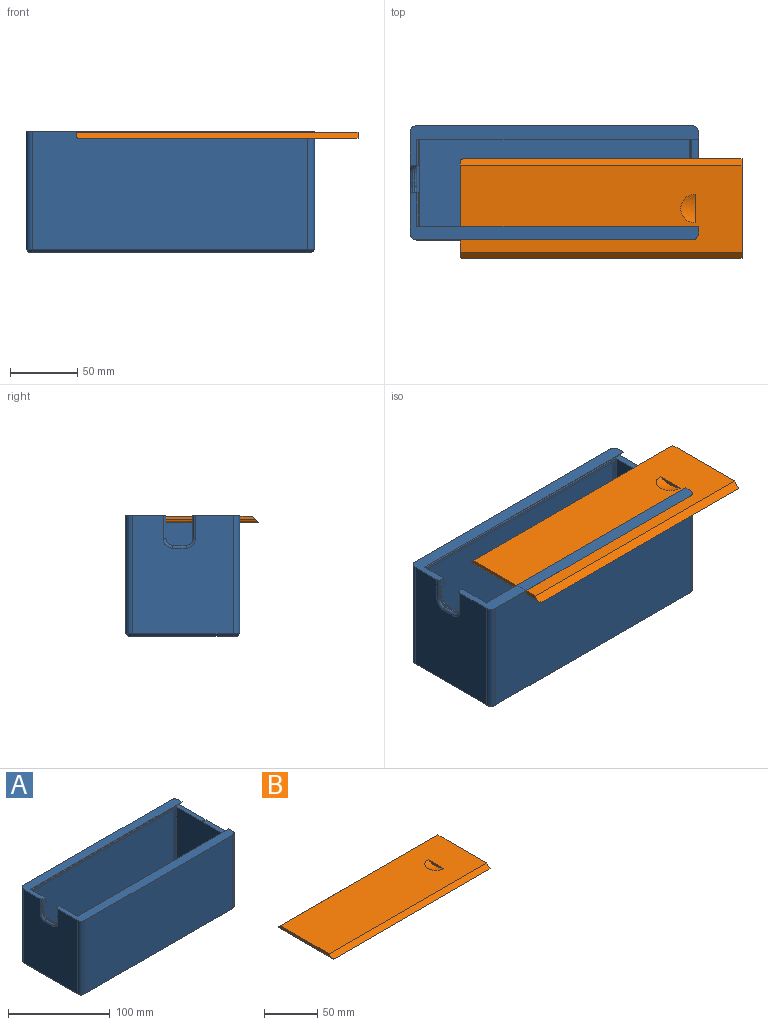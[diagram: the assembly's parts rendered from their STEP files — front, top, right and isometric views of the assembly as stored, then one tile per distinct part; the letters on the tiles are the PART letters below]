
ASSEMBLY  parts=2 mates=1
PART A: 66 faces, bbox 215x85x90 mm
  f0: sphere r=1mm, area 4.8mm2, adj f26,f61,f63,f65
  f1: plane 206.5x30mm, normal (0,0,-1), area 347.2mm2, adj f2,f6,f13,f28,f32,f35,f49,f50
  f2: plane 28.5x2mm, normal (1,0,0), area 57mm2, adj f1,f26,f28,f32
  f3: plane 88x75mm, normal (-1,0,0), area 6040.2mm2, adj f5,f18,f19,f22,f40,f41,f42,f43
  f4: plane 30x5mm, normal (1,0,0), area 137.5mm2, adj f22,f25,f26,f32
  f5: plane 215x30mm, normal (0,0,1), area 2238.4mm2, adj f3,f7,f15,f16,f17,f18,f24,f30
  f6: plane 76x71mm, normal (1,0,0), area 5004.2mm2, adj f1,f27,f35,f36,f37,f38,f39,f46
  f7: plane 25x5mm, normal (1,0,0), area 112.5mm2, adj f5,f24,f26,f30
  f8: plane 203x2mm, normal (0,-1,0), area 406mm2, adj f26,f27,f29,f51
  f9: plane 78x71mm, normal (-1,0,0), area 5538mm2, adj f26,f47,f50,f51
  f10: plane 201x76mm, normal (0,-1,0), area 15276mm2, adj f27,f45,f51,f52
  f11: plane 5x5mm, normal (1,0,0), area 12.5mm2, adj f21,f22,f25
  f12: plane 83x75mm, normal (1,0,0), area 6224mm2, adj f16,f21,f26,f55,f62,f64,f65
  f13: plane 201x76mm, normal (0,1,0), area 15276mm2, adj f1,f48,f49,f50
  f14: plane 211x81mm, normal (0,0,-1), area 17083.3mm2, adj f53,f54,f55,f56,f57,f58,f59,f60
  f15: plane 5x5mm, normal (1,0,0), area 12.5mm2, adj f5,f16,f24
  f16: cylinder r=5mm len=88mm, axis (0,0,-1), area 691.2mm2, adj f5,f12,f15,f17,f53
  f17: plane 205x88mm, normal (0,1,0), area 18040mm2, adj f5,f16,f18,f54
  f18: cylinder r=5mm len=88mm, axis (0,0,-1), area 691.2mm2, adj f3,f5,f17,f56
  f19: cylinder r=5mm len=88mm, axis (0,0,-1), area 691.2mm2, adj f3,f20,f22,f60
  f20: plane 205x88mm, normal (0,-1,0), area 18040mm2, adj f19,f21,f22,f59
  f21: cylinder r=5mm len=88mm, axis (0,0,-1), area 691.2mm2, adj f11,f12,f20,f22,f57
  f22: plane 215x35mm, normal (0,0,1), area 2263.4mm2, adj f3,f4,f11,f19,f20,f21,f25,f32
  f23: plane 201x71mm, normal (0,0,1), area 14271mm2, adj f45,f46,f47,f48
  f24: plane 210x5mm, normal (0,-0.71,-0.71), area 1484.9mm2, adj f5,f7,f15,f26
  f25: plane 210x5mm, normal (0,0.71,-0.71), area 1484.9mm2, adj f4,f11,f22,f26
  f26: plane 210x75mm, normal (0,0,1), area 1061.7mm2, adj f0,f2,f4,f7,f8,f9,f12,f24
  f27: plane 206.5x25mm, normal (0,0,-1), area 339.7mm2, adj f6,f8,f10,f29,f30,f39,f51,f52
  f28: plane 203x2mm, normal (0,1,0), area 406mm2, adj f1,f2,f26,f50
  f29: plane 23.5x2mm, normal (1,0,0), area 47mm2, adj f8,f26,f27,f30
  f30: plane 17.2x4.5mm, normal (0,-1,0), area 34.2mm2, adj f5,f7,f26,f27,f29,f33,f39,f40
  f31: plane 10x1mm, normal (0,0,1), area 10mm2, adj f33,f34,f37,f42
  f32: plane 17.2x4.5mm, normal (0,1,0), area 34.2mm2, adj f1,f2,f4,f22,f26,f34,f35,f44
  f33: cylinder r=5mm len=5mm, axis (1,0,0), area 7.9mm2, adj f30,f31,f38,f41
  f34: cylinder r=5mm len=5mm, axis (-1,0,0), area 7.9mm2, adj f31,f32,f36,f43
  f35: cylinder r=2mm len=10.2mm, axis (0,0,1), area 32mm2, adj f1,f6,f32,f36
  f36: torus R=7mm, axis (-1,0,0), area 28.3mm2, adj f6,f34,f35,f37
  f37: cylinder r=2mm len=10mm, axis (0,-1,0), area 31.4mm2, adj f6,f31,f36,f38
  f38: torus R=7mm, axis (-1,0,0), area 28.3mm2, adj f6,f33,f37,f39
  f39: cylinder r=2mm len=10.2mm, axis (0,0,-1), area 32mm2, adj f6,f27,f30,f38
  f40: cylinder r=2mm len=17.2mm, axis (0,0,1), area 54mm2, adj f3,f5,f30,f41
  f41: torus R=7mm, axis (-1,0,0), area 28.3mm2, adj f3,f33,f40,f42
  f42: cylinder r=2mm len=10mm, axis (0,1,0), area 31.4mm2, adj f3,f31,f41,f43
  f43: torus R=7mm, axis (-1,0,0), area 28.3mm2, adj f3,f34,f42,f44
  f44: cylinder r=2mm len=17.2mm, axis (0,0,-1), area 54mm2, adj f3,f22,f32,f43
  f45: plane 203x2mm, normal (0,-0.71,0.71), area 571.3mm2, adj f10,f23,f46,f47,f51,f52
  f46: plane 73x2mm, normal (0.71,0,0.71), area 203.6mm2, adj f6,f23,f45,f48,f49,f52
  f47: plane 73x2mm, normal (-0.71,0,0.71), area 203.6mm2, adj f9,f23,f45,f48,f50,f51
  f48: plane 203x2mm, normal (0,0.71,0.71), area 571.3mm2, adj f13,f23,f46,f47,f49,f50
  f49: plane 77x2mm, normal (0.71,0.71,0), area 216.4mm2, adj f1,f6,f13,f46,f48
  f50: plane 79x2mm, normal (-0.71,0.71,0), area 217.8mm2, adj f1,f9,f13,f26,f28,f47,f48
  f51: plane 79x2mm, normal (-0.71,-0.71,0), area 217.8mm2, adj f8,f9,f10,f26,f27,f45,f47
  f52: plane 77x2mm, normal (0.71,-0.71,0), area 216.4mm2, adj f6,f10,f27,f45,f46
  f53: cone r=5mm half-angle=45deg, axis (0,0,1), area 17.8mm2, adj f14,f16,f54,f55
  f54: plane 205x2mm, normal (0,0.71,-0.71), area 579.8mm2, adj f14,f17,f53,f56
  f55: plane 75x2mm, normal (0.71,0,-0.71), area 212.1mm2, adj f12,f14,f53,f57
  f56: cone r=5mm half-angle=45deg, axis (0,0,1), area 17.8mm2, adj f14,f18,f54,f58
  f57: cone r=5mm half-angle=45deg, axis (0,0,1), area 17.8mm2, adj f14,f21,f55,f59
  f58: plane 75x2mm, normal (-0.71,0,-0.71), area 212.1mm2, adj f3,f14,f56,f60
  f59: plane 205x2mm, normal (0,-0.71,-0.71), area 579.8mm2, adj f14,f20,f57,f60
  f60: cone r=5mm half-angle=45deg, axis (0,0,1), area 17.8mm2, adj f14,f19,f58,f59
  f61: plane 0.5x0.13mm, normal (1,0,0), area 0mm2, adj f0,f64,f65
  f62: plane 2.46x0.5mm, normal (0,-1,0), area 1.2mm2, adj f12,f26,f63,f65
  f63: plane 0.5x0.13mm, normal (1,0,0), area 0mm2, adj f0,f62,f65
  f64: plane 2.46x0.5mm, normal (0,1,0), area 1.2mm2, adj f12,f26,f61,f65
  f65: plane 2.46x2mm, normal (0,0,1), area 3.8mm2, adj f0,f12,f61,f62,f63,f64
PART B: 10 faces, bbox 210x74x5.4 mm
  f0: plane 210x4.6mm, normal (0,0.71,0.71), area 1364.9mm2, adj f1,f3,f4,f5,f7
  f1: plane 210x64.8mm, normal (0,0,1), area 13433.2mm2, adj f0,f2,f4,f5,f8,f9
  f2: plane 210x4.6mm, normal (0,-0.71,0.71), area 1364.9mm2, adj f1,f3,f4,f5,f7
  f3: plane 208x74mm, normal (0,0,-1), area 15390.2mm2, adj f0,f2,f5,f6,f7
  f4: plane 70x2.6mm, normal (-1,0,0), area 175.2mm2, adj f0,f1,f2,f7
  f5: plane 74x4.6mm, normal (1,0,0), area 319.2mm2, adj f0,f1,f2,f3
  f6: sphere r=0.75mm, area 3.5mm2, adj f3
  f7: cylinder r=2mm len=74mm, axis (0,-1,0), area 227.9mm2, adj f0,f2,f3,f4
  f8: sphere r=23.5mm, area 184.6mm2, adj f1,f9
  f9: plane 21.1x2.5mm, normal (-1,0,0), area 35.6mm2, adj f1,f8
PLACE A t=(-23.12,29.42,-10.19)mm fixed
PLACE B t=(9.16,-89.81,-10.39)mm
MATE slider A.f12 <-> B.f5  axis (1,0,0) through (191.88,52.67,74.81)mm
